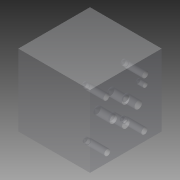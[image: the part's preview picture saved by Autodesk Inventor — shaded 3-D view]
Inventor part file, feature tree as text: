
AUTODESK INVENTOR PART (.ipt)
format: ipt  version: 2014 (Build 180170000, 170)  size: 223,232 bytes
history: native  units: mm
features: other x48, extrude x17, sketch x17
ambient origin geometry x8: Origin, YZ Plane, XZ Plane, XY Plane, X Axis, Y Axis, Z Axis, Center Point
bodies: 实体1 (feature_tree)
feature tree (82):
  extrude  "拉伸1"  Depth=51.0mm
  other  "UCS1"
  other  "UCS2"
  other  "UCS3"
  other  "UCS4"
  other  "UCS5"
  other  "UCS6"
  extrude  "拉伸2"  Depth=30.0mm
  extrude  "拉伸3"  Depth=4.25mm
  extrude  "拉伸4"  Depth=21.5mm
  extrude  "拉伸5"  Depth=0.75mm
  extrude  "拉伸6"  TaperAngle=0.0deg  [1 undecoded]
  extrude  "拉伸7"  Depth=31.75mm
  extrude  "拉伸8"  Depth=18.5mm
  extrude  "拉伸9"  Depth=18.5mm
  extrude  "拉伸10"  Depth=5.0mm
  extrude  "拉伸11"  Depth=16.0mm
  extrude  "拉伸12"  Depth=16.0mm
  extrude  "拉伸13"  Depth=16.0mm
  extrude  "拉伸14"  Depth=16.0mm TaperAngle=0.0deg
  extrude  "拉伸15"  Depth=16.0mm
  extrude  "拉伸16"  Depth=16.0mm
  extrude  "拉伸17"  Depth=16.0mm
  sketch  "草图1"  dims[d0=60.0mm d1=0.0mm]
  sketch  "草图2"  dims[d2=0.0mm d3=0.0mm d4=0.0mm d5=0.0mm d6=0.0mm d7=0.0mm]
  sketch  "草图3"  dims[d8=0.0mm d9=0.0mm d10=0.0mm d11=0.0mm d12=0.0mm d13=0.0mm]
  sketch  "草图4"  dims[d14=0.0mm d15=0.0mm d16=0.0mm d17=0.0mm d18=0.0mm d19=0.0mm]
  sketch  "草图5"  dims[d20=0.0mm d21=0.0mm d22=0.0mm d23=0.0mm d24=0.0mm d25=0.0mm]
  sketch  "草图6"  dims[d26=0.0mm d27=0.0mm d28=0.0mm d29=0.0mm d30=0.0mm d31=0.0mm]
  sketch  "草图7"  dims[d32=0.0mm d33=0.0mm d34=0.0mm d35=0.0mm d36=0.0mm d37=0.0mm d38=51.0mm]
  sketch  "草图8"  dims[d39=43.0mm d40=30.0mm]
  sketch  "草图9"  dims[d41=29.0mm d42=4.25mm]
  sketch  "草图10"  dims[d43=15.5mm d44=21.5mm]
  sketch  "草图11"  dims[d45=40.5mm d46=0.75mm]
  sketch  "草图12"  dims[d47=40.5mm d49=0.0mm]
  sketch  "草图13"  dims[d50=31.0mm d51=31.75mm]
  sketch  "草图14"  dims[d52=18.5mm d53=0.0mm d54=18.5mm d55=-10.297443mm]
  sketch  "草图15"  dims[d56=18.5mm d57=-10.297443mm d58=18.5mm d59=-10.297443mm]
  sketch  "草图17"  dims[d60=18.5mm d61=-10.297443mm d62=5.0mm]
  sketch  "草图18"  dims[d63=16.0mm d64=0.0mm d65=6.3mm d66=25.9mm d67=21.5mm d68=10.7mm d69=0.0mm d70=10.7mm d71=-10.297443mm d72=6.3mm d73=21.5mm d74=5.1mm d75=13.7mm d76=0.0mm d77=13.7mm d78=-10.297443mm d79=6.3mm d80=12.7mm d81=15.5mm d82=11.7mm d83=0.0mm d84=11.7mm d85=-10.297443mm d86=6.3mm d87=15.5mm d88=30.2mm d89=12.7mm d90=0.0mm d91=12.7mm d92=-10.297443mm d106=4.0mm d107=33.0mm d108=31.75mm d109=6.0mm d110=0.0mm d111=6.0mm d112=-10.297443mm]
  other  "UCS1: YZ 平面"
  other  "UCS1: XZ 平面"
  other  "UCS1: XY 平面"
  other  "UCS1: X 轴"
  other  "UCS1: Y 轴"
  other  "UCS1: Z 轴"
  other  "UCS1: 原点"
  other  "UCS2: YZ 平面"
  other  "UCS2: XZ 平面"
  other  "UCS2: XY 平面"
  other  "UCS2: X 轴"
  other  "UCS2: Y 轴"
  other  "UCS2: Z 轴"
  other  "UCS2: 原点"
  other  "UCS3: YZ 平面"
  other  "UCS3: XZ 平面"
  other  "UCS3: XY 平面"
  other  "UCS3: X 轴"
  other  "UCS3: Y 轴"
  other  "UCS3: Z 轴"
  other  "UCS3: 原点"
  other  "UCS4: YZ 平面"
  other  "UCS4: XZ 平面"
  other  "UCS4: XY 平面"
  other  "UCS4: X 轴"
  other  "UCS4: Y 轴"
  other  "UCS4: Z 轴"
  other  "UCS4: 原点"
  other  "UCS5: YZ 平面"
  other  "UCS5: XZ 平面"
  other  "UCS5: XY 平面"
  other  "UCS5: X 轴"
  other  "UCS5: Y 轴"
  other  "UCS5: Z 轴"
  other  "UCS5: 原点"
  other  "UCS6: YZ 平面"
  other  "UCS6: XZ 平面"
  other  "UCS6: XY 平面"
  other  "UCS6: X 轴"
  other  "UCS6: Y 轴"
  other  "UCS6: Z 轴"
  other  "UCS6: 原点"
note: 1 required parameter value undecoded (feature->parameter linkage not recoverable at this tier; creation-order binding heuristic only, values carry confidence <= 0.55)
